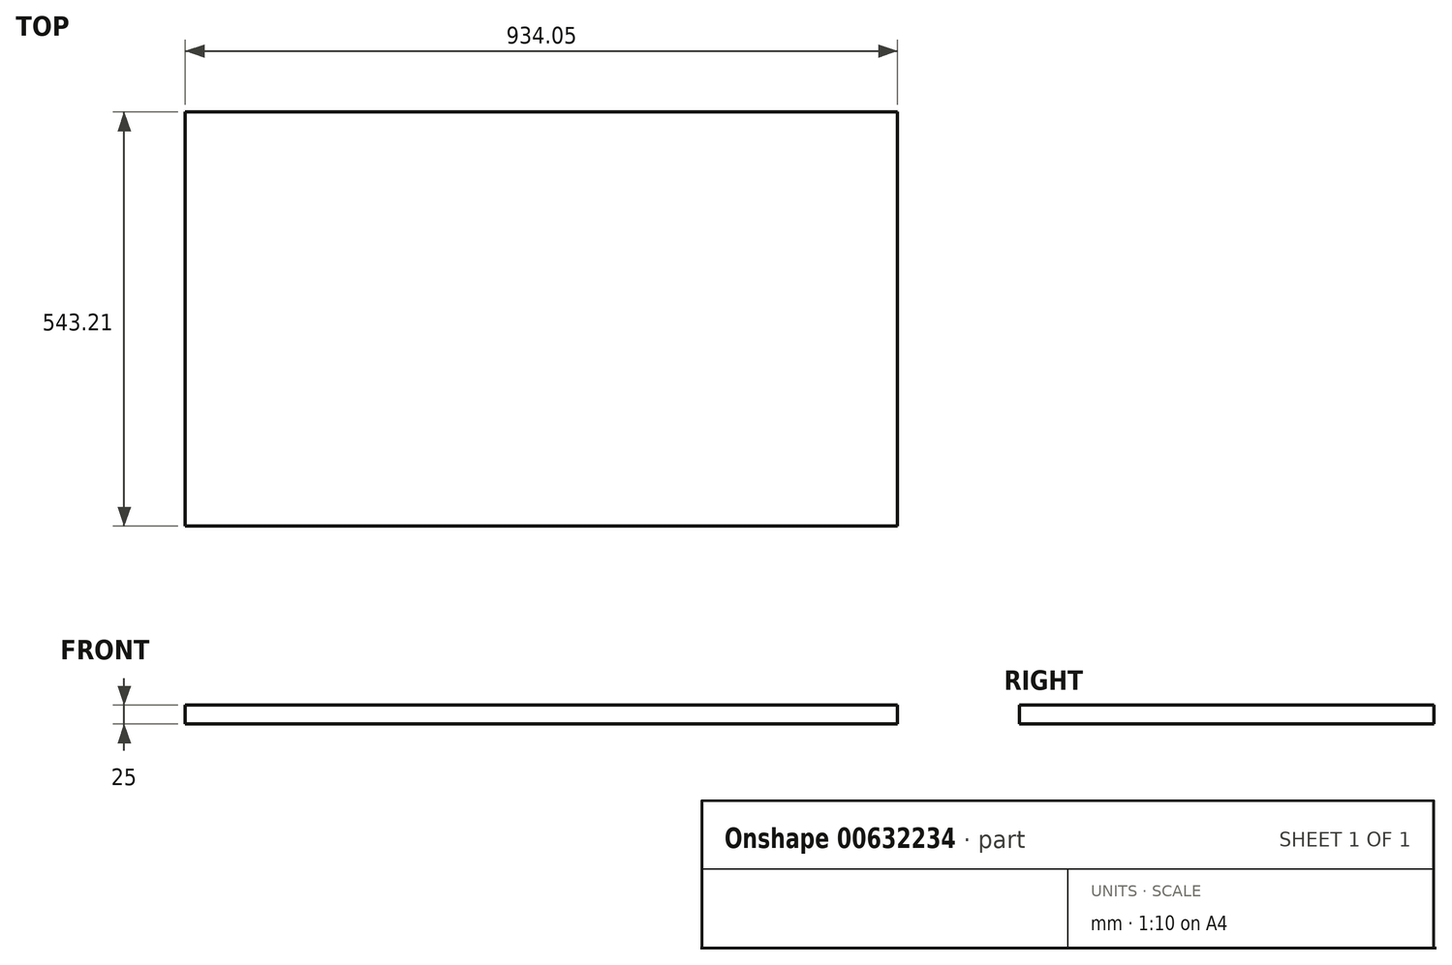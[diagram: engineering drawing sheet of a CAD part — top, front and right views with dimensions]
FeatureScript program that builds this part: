
annotation { "Feature Type Name" : "Feature", "Feature Type Description" : "" }
export const myFeature = defineFeature(function(context is Context, id is Id, definition is map)
    precondition{}
    {
        {
            var Q0;
            Q0=qCreatedBy(makeId("Top.planeOp"),FACE);
            var sketch = newSketch(context, id + "F0", { "sketchPlane" : qUnion([Q0])});
            skLineSegment(sketch, "E0.bottom", {"start": v(67.5, 70.89) * mm, "end": v(-66.56, 70.89) * mm});
            skLineSegment(sketch, "E0.top", {"start": v(67.5, -72.32) * mm, "end": v(-66.56, -72.32) * mm});
            skLineSegment(sketch, "E0.left", {"start": v(67.5, 70.89) * mm, "end": v(67.5, -72.32) * mm});
            skLineSegment(sketch, "E0.right", {"start": v(-66.56, 70.89) * mm, "end": v(-66.56, -72.32) * mm});
            skSolve(sketch);
        }
        {
            var Q0;
            Q0 = qSketchRegion(id + "F0", true);
            extrude(context, id + "F1", {"entities" : qUnion([Q0]), "depth" : 25 * mm, "offsetDistance" : 25 * mm});
        }
        {
            var Q0;
            Q0=makeQuery(id+"F1.opExtrude","SWEPT_FACE",FACE,{"disambiguationData":[OSD([sQuery(id+"F0.wireOp",EDGE,"E0.left")])]});
            extrude(context, id + "F2", {"entities" : qUnion([Q0]), "operationType" : NewBodyOperationType.ADD, "depth" : 800 * mm, "offsetDistance" : 25 * mm});
        }
        {
            var Q0;
            {var subQ0=sQuery(id+"F0.wireOp",EDGE,"E0.bottom");Q0=makeQuery(id+"F2.boolean.opBoolean","MERGE",FACE,{"derivedFrom":[makeQuery(id+"F1.opExtrude","SWEPT_FACE",FACE,{"disambiguationData":[OSD([subQ0])]}),makeQuery(id+"F2.opExtrude","SWEPT_FACE",FACE,{"disambiguationData":[OSD([subQ0,sQuery(id+"F0.wireOp",EDGE,"E0.left")])]})]});}
            extrude(context, id + "F3", {"entities" : qUnion([Q0]), "operationType" : NewBodyOperationType.ADD, "depth" : 400 * mm, "offsetDistance" : 25 * mm});
        }
    });
